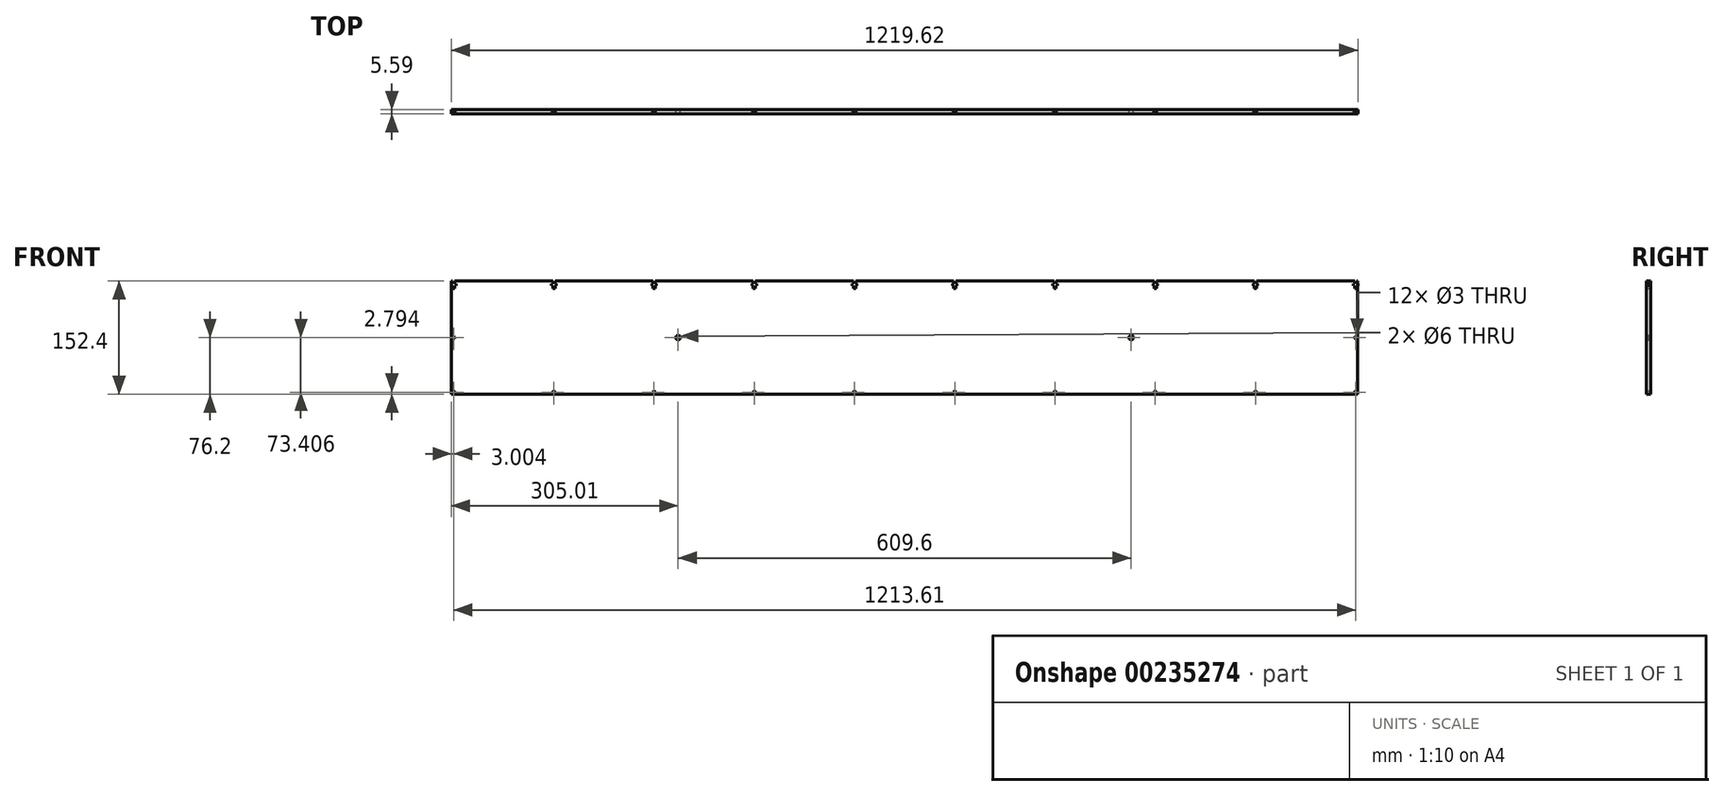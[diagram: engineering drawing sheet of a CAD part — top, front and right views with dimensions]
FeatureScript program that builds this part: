
annotation { "Feature Type Name" : "Feature", "Feature Type Description" : "" }
export const myFeature = defineFeature(function(context is Context, id is Id, definition is map)
    precondition{}
    {
        {
            var Q0;
            Q0=qCreatedBy(makeId("Front.planeOp"),FACE);
            var sketch = newSketch(context, id + "F0", { "sketchPlane" : qUnion([Q0])});
            skLineSegment(sketch, "E0.bottom", {"start": v(609.6, -76.2) * mm, "end": v(-609.6, -76.2) * mm});
            skLineSegment(sketch, "E0.top", {"start": v(609.6, 76.2) * mm, "end": v(608.3, 76.2) * mm});
            skLineSegment(sketch, "E0.left", {"start": v(609.6, -76.2) * mm, "end": v(609.6, 76.2) * mm});
            skLineSegment(sketch, "E0.right", {"start": v(-609.6, -76.2) * mm, "end": v(-609.6, 76.2) * mm});
            skPoint(sketch, "E0.middle", {"position": v(0, 0) * mm});
            skLineSegment(sketch, "E1", {"start": v(-606.8, 76.2) * mm, "end": v(-606.8, 73.4) * mm, "construction": true});
            skLineSegment(sketch, "E2", {"start": v(-608.3, 76.2) * mm, "end": v(-608.3, 72.2) * mm});
            skLineSegment(sketch, "E3", {"start": v(-608.3, 72.2) * mm, "end": v(-609.8, 72.2) * mm});
            skLineSegment(sketch, "E4", {"start": v(-609.8, 72.2) * mm, "end": v(-609.8, 70.2) * mm});
            skLineSegment(sketch, "E5", {"start": v(-609.8, 70.2) * mm, "end": v(-608.3, 70.2) * mm});
            skLineSegment(sketch, "E6", {"start": v(-608.3, 70.2) * mm, "end": v(-608.3, 66.2) * mm});
            skLineSegment(sketch, "E7", {"start": v(-608.3, 66.2) * mm, "end": v(-606.8, 66.2) * mm});
            skLineSegment(sketch, "E8.MirrorCS", {"start": v(-605.3, 76.2) * mm, "end": v(-605.3, 72.2) * mm});
            skLineSegment(sketch, "E9.MirrorCS", {"start": v(-605.3, 72.2) * mm, "end": v(-603.8, 72.2) * mm});
            skLineSegment(sketch, "E10.MirrorCS", {"start": v(-603.8, 72.2) * mm, "end": v(-603.8, 70.2) * mm});
            skLineSegment(sketch, "E11.MirrorCS", {"start": v(-603.8, 70.2) * mm, "end": v(-605.3, 70.2) * mm});
            skLineSegment(sketch, "E12.MirrorCS", {"start": v(-605.3, 70.2) * mm, "end": v(-605.3, 66.2) * mm});
            skLineSegment(sketch, "E13.MirrorCS", {"start": v(-605.3, 66.2) * mm, "end": v(-606.8, 66.2) * mm});
            skLineSegment(sketch, "E14.trimOffspring", {"start": v(-608.3, 76.2) * mm, "end": v(-609.6, 76.2) * mm});
            skLineSegment(sketch, "E15.1.0.0", {"start": v(-473.46, 76.2) * mm, "end": v(-473.46, 72.2) * mm});
            skLineSegment(sketch, "E15.1.0.1", {"start": v(-470.46, 76.2) * mm, "end": v(-470.46, 72.2) * mm});
            skLineSegment(sketch, "E15.1.0.2", {"start": v(-468.96, 72.2) * mm, "end": v(-468.96, 70.2) * mm});
            skLineSegment(sketch, "E15.1.0.3", {"start": v(-470.46, 70.2) * mm, "end": v(-470.46, 66.2) * mm});
            skLineSegment(sketch, "E15.1.0.4", {"start": v(-471.96, 76.2) * mm, "end": v(-471.96, 73.4) * mm, "construction": true});
            skLineSegment(sketch, "E15.1.0.5", {"start": v(-474.96, 72.2) * mm, "end": v(-474.96, 70.2) * mm});
            skLineSegment(sketch, "E15.1.0.6", {"start": v(-473.46, 70.2) * mm, "end": v(-473.46, 66.2) * mm});
            skLineSegment(sketch, "E15.1.0.7", {"start": v(-473.46, 72.2) * mm, "end": v(-474.96, 72.2) * mm});
            skLineSegment(sketch, "E15.1.0.8", {"start": v(-473.46, 66.2) * mm, "end": v(-471.96, 66.2) * mm});
            skLineSegment(sketch, "E15.1.0.9", {"start": v(-470.46, 72.2) * mm, "end": v(-468.96, 72.2) * mm});
            skLineSegment(sketch, "E15.1.0.10", {"start": v(-468.96, 70.2) * mm, "end": v(-470.46, 70.2) * mm});
            skLineSegment(sketch, "E15.1.0.11", {"start": v(-470.46, 66.2) * mm, "end": v(-471.96, 66.2) * mm});
            skLineSegment(sketch, "E15.1.0.12", {"start": v(-474.96, 70.2) * mm, "end": v(-473.46, 70.2) * mm});
            skLineSegment(sketch, "E15.2.0.0", {"start": v(-338.61, 76.2) * mm, "end": v(-338.61, 72.2) * mm});
            skLineSegment(sketch, "E15.2.0.1", {"start": v(-335.61, 76.2) * mm, "end": v(-335.61, 72.2) * mm});
            skLineSegment(sketch, "E15.2.0.2", {"start": v(-334.11, 72.2) * mm, "end": v(-334.11, 70.2) * mm});
            skLineSegment(sketch, "E15.2.0.3", {"start": v(-335.61, 70.2) * mm, "end": v(-335.61, 66.2) * mm});
            skLineSegment(sketch, "E15.2.0.4", {"start": v(-337.11, 76.2) * mm, "end": v(-337.11, 73.4) * mm, "construction": true});
            skLineSegment(sketch, "E15.2.0.5", {"start": v(-340.11, 72.2) * mm, "end": v(-340.11, 70.2) * mm});
            skLineSegment(sketch, "E15.2.0.6", {"start": v(-338.61, 70.2) * mm, "end": v(-338.61, 66.2) * mm});
            skLineSegment(sketch, "E15.2.0.7", {"start": v(-338.61, 72.2) * mm, "end": v(-340.11, 72.2) * mm});
            skLineSegment(sketch, "E15.2.0.8", {"start": v(-338.61, 66.2) * mm, "end": v(-337.11, 66.2) * mm});
            skLineSegment(sketch, "E15.2.0.9", {"start": v(-335.61, 72.2) * mm, "end": v(-334.11, 72.2) * mm});
            skLineSegment(sketch, "E15.2.0.10", {"start": v(-334.11, 70.2) * mm, "end": v(-335.61, 70.2) * mm});
            skLineSegment(sketch, "E15.2.0.11", {"start": v(-335.61, 66.2) * mm, "end": v(-337.11, 66.2) * mm});
            skLineSegment(sketch, "E15.2.0.12", {"start": v(-340.11, 70.2) * mm, "end": v(-338.61, 70.2) * mm});
            skLineSegment(sketch, "E15.3.0.0", {"start": v(-203.77, 76.2) * mm, "end": v(-203.77, 72.2) * mm});
            skLineSegment(sketch, "E15.3.0.1", {"start": v(-200.77, 76.2) * mm, "end": v(-200.77, 72.2) * mm});
            skLineSegment(sketch, "E15.3.0.2", {"start": v(-199.27, 72.2) * mm, "end": v(-199.27, 70.2) * mm});
            skLineSegment(sketch, "E15.3.0.3", {"start": v(-200.77, 70.2) * mm, "end": v(-200.77, 66.2) * mm});
            skLineSegment(sketch, "E15.3.0.4", {"start": v(-202.27, 76.2) * mm, "end": v(-202.27, 73.4) * mm, "construction": true});
            skLineSegment(sketch, "E15.3.0.5", {"start": v(-205.27, 72.2) * mm, "end": v(-205.27, 70.2) * mm});
            skLineSegment(sketch, "E15.3.0.6", {"start": v(-203.77, 70.2) * mm, "end": v(-203.77, 66.2) * mm});
            skLineSegment(sketch, "E15.3.0.7", {"start": v(-203.77, 72.2) * mm, "end": v(-205.27, 72.2) * mm});
            skLineSegment(sketch, "E15.3.0.8", {"start": v(-203.77, 66.2) * mm, "end": v(-202.27, 66.2) * mm});
            skLineSegment(sketch, "E15.3.0.9", {"start": v(-200.77, 72.2) * mm, "end": v(-199.27, 72.2) * mm});
            skLineSegment(sketch, "E15.3.0.10", {"start": v(-199.27, 70.2) * mm, "end": v(-200.77, 70.2) * mm});
            skLineSegment(sketch, "E15.3.0.11", {"start": v(-200.77, 66.2) * mm, "end": v(-202.27, 66.2) * mm});
            skLineSegment(sketch, "E15.3.0.12", {"start": v(-205.27, 70.2) * mm, "end": v(-203.77, 70.2) * mm});
            skLineSegment(sketch, "E15.4.0.0", {"start": v(-68.92, 76.2) * mm, "end": v(-68.92, 72.2) * mm});
            skLineSegment(sketch, "E15.4.0.1", {"start": v(-65.92, 76.2) * mm, "end": v(-65.92, 72.2) * mm});
            skLineSegment(sketch, "E15.4.0.2", {"start": v(-64.42, 72.2) * mm, "end": v(-64.42, 70.2) * mm});
            skLineSegment(sketch, "E15.4.0.3", {"start": v(-65.92, 70.2) * mm, "end": v(-65.92, 66.2) * mm});
            skLineSegment(sketch, "E15.4.0.4", {"start": v(-67.42, 76.2) * mm, "end": v(-67.42, 73.4) * mm, "construction": true});
            skLineSegment(sketch, "E15.4.0.5", {"start": v(-70.42, 72.2) * mm, "end": v(-70.42, 70.2) * mm});
            skLineSegment(sketch, "E15.4.0.6", {"start": v(-68.92, 70.2) * mm, "end": v(-68.92, 66.2) * mm});
            skLineSegment(sketch, "E15.4.0.7", {"start": v(-68.92, 72.2) * mm, "end": v(-70.42, 72.2) * mm});
            skLineSegment(sketch, "E15.4.0.8", {"start": v(-68.92, 66.2) * mm, "end": v(-67.42, 66.2) * mm});
            skLineSegment(sketch, "E15.4.0.9", {"start": v(-65.92, 72.2) * mm, "end": v(-64.42, 72.2) * mm});
            skLineSegment(sketch, "E15.4.0.10", {"start": v(-64.42, 70.2) * mm, "end": v(-65.92, 70.2) * mm});
            skLineSegment(sketch, "E15.4.0.11", {"start": v(-65.92, 66.2) * mm, "end": v(-67.42, 66.2) * mm});
            skLineSegment(sketch, "E15.4.0.12", {"start": v(-70.42, 70.2) * mm, "end": v(-68.92, 70.2) * mm});
            skLineSegment(sketch, "E15.5.0.0", {"start": v(65.92, 76.2) * mm, "end": v(65.92, 72.2) * mm});
            skLineSegment(sketch, "E15.5.0.1", {"start": v(68.92, 76.2) * mm, "end": v(68.92, 72.2) * mm});
            skLineSegment(sketch, "E15.5.0.2", {"start": v(70.42, 72.2) * mm, "end": v(70.42, 70.2) * mm});
            skLineSegment(sketch, "E15.5.0.3", {"start": v(68.92, 70.2) * mm, "end": v(68.92, 66.2) * mm});
            skLineSegment(sketch, "E15.5.0.4", {"start": v(67.42, 76.2) * mm, "end": v(67.42, 73.4) * mm, "construction": true});
            skLineSegment(sketch, "E15.5.0.5", {"start": v(64.42, 72.2) * mm, "end": v(64.42, 70.2) * mm});
            skLineSegment(sketch, "E15.5.0.6", {"start": v(65.92, 70.2) * mm, "end": v(65.92, 66.2) * mm});
            skLineSegment(sketch, "E15.5.0.7", {"start": v(65.92, 72.2) * mm, "end": v(64.42, 72.2) * mm});
            skLineSegment(sketch, "E15.5.0.8", {"start": v(65.92, 66.2) * mm, "end": v(67.42, 66.2) * mm});
            skLineSegment(sketch, "E15.5.0.9", {"start": v(68.92, 72.2) * mm, "end": v(70.42, 72.2) * mm});
            skLineSegment(sketch, "E15.5.0.10", {"start": v(70.42, 70.2) * mm, "end": v(68.92, 70.2) * mm});
            skLineSegment(sketch, "E15.5.0.11", {"start": v(68.92, 66.2) * mm, "end": v(67.42, 66.2) * mm});
            skLineSegment(sketch, "E15.5.0.12", {"start": v(64.42, 70.2) * mm, "end": v(65.92, 70.2) * mm});
            skLineSegment(sketch, "E15.6.0.0", {"start": v(200.77, 76.2) * mm, "end": v(200.77, 72.2) * mm});
            skLineSegment(sketch, "E15.6.0.1", {"start": v(203.77, 76.2) * mm, "end": v(203.77, 72.2) * mm});
            skLineSegment(sketch, "E15.6.0.2", {"start": v(205.27, 72.2) * mm, "end": v(205.27, 70.2) * mm});
            skLineSegment(sketch, "E15.6.0.3", {"start": v(203.77, 70.2) * mm, "end": v(203.77, 66.2) * mm});
            skLineSegment(sketch, "E15.6.0.4", {"start": v(202.27, 76.2) * mm, "end": v(202.27, 73.4) * mm, "construction": true});
            skLineSegment(sketch, "E15.6.0.5", {"start": v(199.27, 72.2) * mm, "end": v(199.27, 70.2) * mm});
            skLineSegment(sketch, "E15.6.0.6", {"start": v(200.77, 70.2) * mm, "end": v(200.77, 66.2) * mm});
            skLineSegment(sketch, "E15.6.0.7", {"start": v(200.77, 72.2) * mm, "end": v(199.27, 72.2) * mm});
            skLineSegment(sketch, "E15.6.0.8", {"start": v(200.77, 66.2) * mm, "end": v(202.27, 66.2) * mm});
            skLineSegment(sketch, "E15.6.0.9", {"start": v(203.77, 72.2) * mm, "end": v(205.27, 72.2) * mm});
            skLineSegment(sketch, "E15.6.0.10", {"start": v(205.27, 70.2) * mm, "end": v(203.77, 70.2) * mm});
            skLineSegment(sketch, "E15.6.0.11", {"start": v(203.77, 66.2) * mm, "end": v(202.27, 66.2) * mm});
            skLineSegment(sketch, "E15.6.0.12", {"start": v(199.27, 70.2) * mm, "end": v(200.77, 70.2) * mm});
            skLineSegment(sketch, "E15.7.0.0", {"start": v(335.62, 76.2) * mm, "end": v(335.62, 72.2) * mm});
            skLineSegment(sketch, "E15.7.0.1", {"start": v(338.62, 76.2) * mm, "end": v(338.62, 72.2) * mm});
            skLineSegment(sketch, "E15.7.0.2", {"start": v(340.12, 72.2) * mm, "end": v(340.12, 70.2) * mm});
            skLineSegment(sketch, "E15.7.0.3", {"start": v(338.62, 70.2) * mm, "end": v(338.62, 66.2) * mm});
            skLineSegment(sketch, "E15.7.0.4", {"start": v(337.12, 76.2) * mm, "end": v(337.12, 73.4) * mm, "construction": true});
            skLineSegment(sketch, "E15.7.0.5", {"start": v(334.12, 72.2) * mm, "end": v(334.12, 70.2) * mm});
            skLineSegment(sketch, "E15.7.0.6", {"start": v(335.62, 70.2) * mm, "end": v(335.62, 66.2) * mm});
            skLineSegment(sketch, "E15.7.0.7", {"start": v(335.62, 72.2) * mm, "end": v(334.12, 72.2) * mm});
            skLineSegment(sketch, "E15.7.0.8", {"start": v(335.62, 66.2) * mm, "end": v(337.12, 66.2) * mm});
            skLineSegment(sketch, "E15.7.0.9", {"start": v(338.62, 72.2) * mm, "end": v(340.12, 72.2) * mm});
            skLineSegment(sketch, "E15.7.0.10", {"start": v(340.12, 70.2) * mm, "end": v(338.62, 70.2) * mm});
            skLineSegment(sketch, "E15.7.0.11", {"start": v(338.62, 66.2) * mm, "end": v(337.12, 66.2) * mm});
            skLineSegment(sketch, "E15.7.0.12", {"start": v(334.12, 70.2) * mm, "end": v(335.62, 70.2) * mm});
            skLineSegment(sketch, "E15.8.0.0", {"start": v(470.46, 76.2) * mm, "end": v(470.46, 72.2) * mm});
            skLineSegment(sketch, "E15.8.0.1", {"start": v(473.46, 76.2) * mm, "end": v(473.46, 72.2) * mm});
            skLineSegment(sketch, "E15.8.0.2", {"start": v(474.96, 72.2) * mm, "end": v(474.96, 70.2) * mm});
            skLineSegment(sketch, "E15.8.0.3", {"start": v(473.46, 70.2) * mm, "end": v(473.46, 66.2) * mm});
            skLineSegment(sketch, "E15.8.0.4", {"start": v(471.96, 76.2) * mm, "end": v(471.96, 73.4) * mm, "construction": true});
            skLineSegment(sketch, "E15.8.0.5", {"start": v(468.96, 72.2) * mm, "end": v(468.96, 70.2) * mm});
            skLineSegment(sketch, "E15.8.0.6", {"start": v(470.46, 70.2) * mm, "end": v(470.46, 66.2) * mm});
            skLineSegment(sketch, "E15.8.0.7", {"start": v(470.46, 72.2) * mm, "end": v(468.96, 72.2) * mm});
            skLineSegment(sketch, "E15.8.0.8", {"start": v(470.46, 66.2) * mm, "end": v(471.96, 66.2) * mm});
            skLineSegment(sketch, "E15.8.0.9", {"start": v(473.46, 72.2) * mm, "end": v(474.96, 72.2) * mm});
            skLineSegment(sketch, "E15.8.0.10", {"start": v(474.96, 70.2) * mm, "end": v(473.46, 70.2) * mm});
            skLineSegment(sketch, "E15.8.0.11", {"start": v(473.46, 66.2) * mm, "end": v(471.96, 66.2) * mm});
            skLineSegment(sketch, "E15.8.0.12", {"start": v(468.96, 70.2) * mm, "end": v(470.46, 70.2) * mm});
            skLineSegment(sketch, "E15.9.0.0", {"start": v(605.3, 76.2) * mm, "end": v(605.3, 72.2) * mm});
            skLineSegment(sketch, "E15.9.0.1", {"start": v(608.3, 76.2) * mm, "end": v(608.3, 72.2) * mm});
            skLineSegment(sketch, "E15.9.0.2", {"start": v(609.8, 72.2) * mm, "end": v(609.8, 70.2) * mm});
            skLineSegment(sketch, "E15.9.0.3", {"start": v(608.3, 70.2) * mm, "end": v(608.3, 66.2) * mm});
            skLineSegment(sketch, "E15.9.0.4", {"start": v(606.8, 76.2) * mm, "end": v(606.8, 73.4) * mm, "construction": true});
            skLineSegment(sketch, "E15.9.0.5", {"start": v(603.8, 72.2) * mm, "end": v(603.8, 70.2) * mm});
            skLineSegment(sketch, "E15.9.0.6", {"start": v(605.3, 70.2) * mm, "end": v(605.3, 66.2) * mm});
            skLineSegment(sketch, "E15.9.0.7", {"start": v(605.3, 72.2) * mm, "end": v(603.8, 72.2) * mm});
            skLineSegment(sketch, "E15.9.0.8", {"start": v(605.3, 66.2) * mm, "end": v(606.8, 66.2) * mm});
            skLineSegment(sketch, "E15.9.0.9", {"start": v(608.3, 72.2) * mm, "end": v(609.8, 72.2) * mm});
            skLineSegment(sketch, "E15.9.0.10", {"start": v(609.8, 70.2) * mm, "end": v(608.3, 70.2) * mm});
            skLineSegment(sketch, "E15.9.0.11", {"start": v(608.3, 66.2) * mm, "end": v(606.8, 66.2) * mm});
            skLineSegment(sketch, "E15.9.0.12", {"start": v(603.8, 70.2) * mm, "end": v(605.3, 70.2) * mm});
            skLineSegment(sketch, "E15.direction1", {"start": v(-608.3, 66.2) * mm, "end": v(-473.46, 66.2) * mm, "construction": true});
            skLineSegment(sketch, "E16.trimOffspring", {"start": v(605.3, 76.2) * mm, "end": v(473.46, 76.2) * mm});
            skLineSegment(sketch, "E17.trimOffspring", {"start": v(470.46, 76.2) * mm, "end": v(338.62, 76.2) * mm});
            skLineSegment(sketch, "E18.trimOffspring", {"start": v(335.62, 76.2) * mm, "end": v(203.77, 76.2) * mm});
            skLineSegment(sketch, "E19.trimOffspring", {"start": v(200.77, 76.2) * mm, "end": v(68.92, 76.2) * mm});
            skLineSegment(sketch, "E20.trimOffspring", {"start": v(65.92, 76.2) * mm, "end": v(-65.92, 76.2) * mm});
            skLineSegment(sketch, "E21.trimOffspring", {"start": v(-68.92, 76.2) * mm, "end": v(-200.77, 76.2) * mm});
            skLineSegment(sketch, "E22.trimOffspring", {"start": v(-203.77, 76.2) * mm, "end": v(-335.61, 76.2) * mm});
            skLineSegment(sketch, "E23.trimOffspring", {"start": v(-338.61, 76.2) * mm, "end": v(-470.46, 76.2) * mm});
            skLineSegment(sketch, "E24.trimOffspring", {"start": v(-473.46, 76.2) * mm, "end": v(-605.3, 76.2) * mm});
            skLineSegment(sketch, "E25.MirrorCS", {"start": v(-606.8, -76.2) * mm, "end": v(-606.8, -73.4) * mm, "construction": true});
            skCircle(sketch, "E26", {"center": v(-606.8, -73.4) * mm, "radius": 1.5 * mm});
            skCircle(sketch, "E27.1.0.0", {"center": v(-471.96, -73.4) * mm, "radius": 1.5 * mm});
            skCircle(sketch, "E27.2.0.0", {"center": v(-337.11, -73.4) * mm, "radius": 1.5 * mm});
            skCircle(sketch, "E27.3.0.0", {"center": v(-202.27, -73.4) * mm, "radius": 1.5 * mm});
            skCircle(sketch, "E27.4.0.0", {"center": v(-67.42, -73.4) * mm, "radius": 1.5 * mm});
            skCircle(sketch, "E27.5.0.0", {"center": v(67.42, -73.4) * mm, "radius": 1.5 * mm});
            skCircle(sketch, "E27.6.0.0", {"center": v(202.27, -73.4) * mm, "radius": 1.5 * mm});
            skCircle(sketch, "E27.7.0.0", {"center": v(337.12, -73.4) * mm, "radius": 1.5 * mm});
            skCircle(sketch, "E27.8.0.0", {"center": v(471.96, -73.4) * mm, "radius": 1.5 * mm});
            skCircle(sketch, "E27.9.0.0", {"center": v(606.8, -73.4) * mm, "radius": 1.5 * mm});
            skLineSegment(sketch, "E27.direction1", {"start": v(-606.8, -73.4) * mm, "end": v(-471.96, -73.4) * mm, "construction": true});
            skPoint(sketch, "E28.endSnap0", {"position": v(-609.6, 0) * mm});
            skCircle(sketch, "E29", {"center": v(-606.8, 0) * mm, "radius": 1.5 * mm});
            skLineSegment(sketch, "E30", {"start": v(0, 0) * mm, "end": v(0, 48.8) * mm, "construction": true});
            skCircle(sketch, "E31.MirrorC", {"center": v(606.8, 0) * mm, "radius": 1.5 * mm});
            skLineSegment(sketch, "E32", {"start": v(0, 0) * mm, "end": v(609.6, 0) * mm, "construction": true});
            skCircle(sketch, "E33", {"center": v(304.8, 0) * mm, "radius": 3 * mm});
            skCircle(sketch, "E34.MirrorC", {"center": v(-304.8, 0) * mm, "radius": 3 * mm});
            skSolve(sketch);
        }
        {
            var Q0;
            Q0 = qSketchRegion(id + "F0", true);
            extrude(context, id + "F1", {"entities" : qUnion([Q0]), "depth" : 5.6 * mm});
        }
    });
